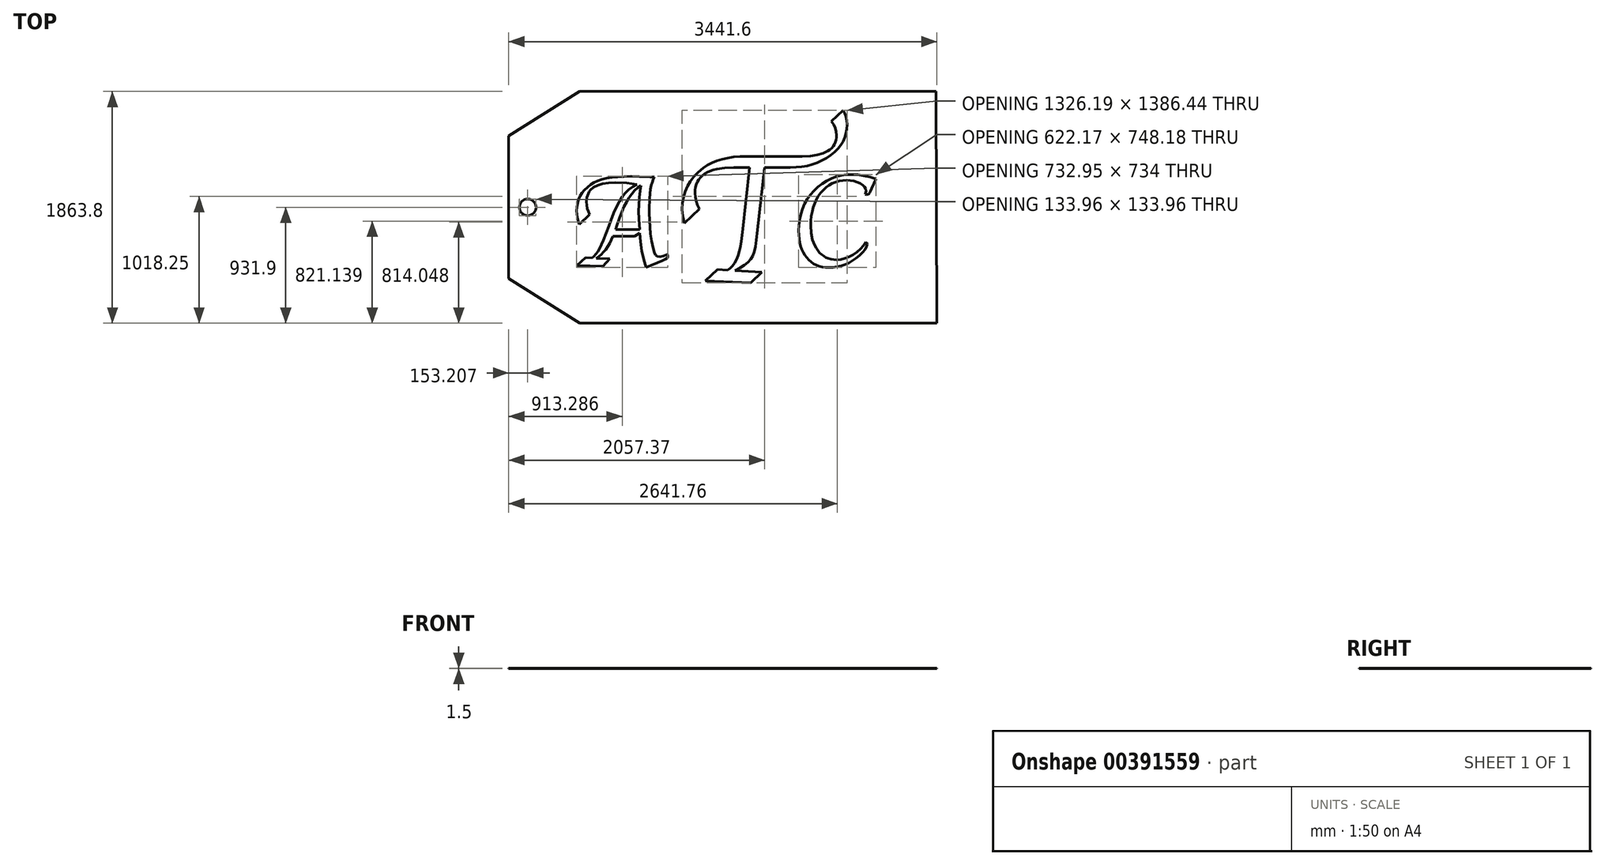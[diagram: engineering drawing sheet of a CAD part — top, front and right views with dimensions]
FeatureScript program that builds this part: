
annotation { "Feature Type Name" : "Feature", "Feature Type Description" : "" }
export const myFeature = defineFeature(function(context is Context, id is Id, definition is map)
    precondition{}
    {
        {
            var Q0;
            Q0=qCreatedBy(makeId("Top.planeOp"),FACE);
            var sketch = newSketch(context, id + "F0", { "sketchPlane" : qUnion([Q0])});
            skLineSegment(sketch, "E0", {"start": v(-1148.46, 931.9) * mm, "end": v(-1720.8, 573.48) * mm});
            skLineSegment(sketch, "E1", {"start": v(-1720.8, 573.48) * mm, "end": v(-1720.8, -573.48) * mm});
            skLineSegment(sketch, "E2", {"start": v(-1720.8, -573.48) * mm, "end": v(-1148.46, -931.9) * mm});
            skLineSegment(sketch, "E3", {"start": v(-1148.46, -931.9) * mm, "end": v(1720.8, -931.9) * mm});
            skLineSegment(sketch, "E4", {"start": v(1720.8, -931.9) * mm, "end": v(1714.81, 931.9) * mm});
            skLineSegment(sketch, "E5", {"start": v(1714.81, 931.9) * mm, "end": v(-1148.46, 931.9) * mm});
            skLineSegment(sketch, "E6", {"start": v(966.93, 779.57) * mm, "end": v(981.25, 755.67) * mm});
            skLineSegment(sketch, "E7", {"start": v(981.25, 755.67) * mm, "end": v(991.48, 728.62) * mm});
            skLineSegment(sketch, "E8", {"start": v(991.48, 728.62) * mm, "end": v(997.62, 698.4) * mm});
            skLineSegment(sketch, "E9", {"start": v(997.62, 698.4) * mm, "end": v(999.66, 665.03) * mm});
            skLineSegment(sketch, "E10", {"start": v(999.66, 665.03) * mm, "end": v(997.6, 629.13) * mm});
            skLineSegment(sketch, "E11", {"start": v(997.6, 629.13) * mm, "end": v(991.39, 594.7) * mm});
            skLineSegment(sketch, "E12", {"start": v(991.39, 594.7) * mm, "end": v(981.04, 561.72) * mm});
            skLineSegment(sketch, "E13", {"start": v(981.04, 561.72) * mm, "end": v(966.56, 530.2) * mm});
            skLineSegment(sketch, "E14", {"start": v(966.56, 530.2) * mm, "end": v(947.94, 500.17) * mm});
            skLineSegment(sketch, "E15", {"start": v(947.94, 500.17) * mm, "end": v(925.18, 471.59) * mm});
            skLineSegment(sketch, "E16", {"start": v(925.18, 471.59) * mm, "end": v(898.29, 444.47) * mm});
            skLineSegment(sketch, "E17", {"start": v(898.29, 444.47) * mm, "end": v(867.26, 418.82) * mm});
            skLineSegment(sketch, "E18", {"start": v(867.26, 418.82) * mm, "end": v(833.37, 395.64) * mm});
            skLineSegment(sketch, "E19", {"start": v(833.37, 395.64) * mm, "end": v(797.53, 375.54) * mm});
            skLineSegment(sketch, "E20", {"start": v(797.53, 375.54) * mm, "end": v(759.73, 358.54) * mm});
            skLineSegment(sketch, "E21", {"start": v(759.73, 358.54) * mm, "end": v(719.99, 344.63) * mm});
            skLineSegment(sketch, "E22", {"start": v(719.99, 344.63) * mm, "end": v(678.3, 333.81) * mm});
            skLineSegment(sketch, "E23", {"start": v(678.3, 333.81) * mm, "end": v(634.64, 326.09) * mm});
            skLineSegment(sketch, "E24", {"start": v(634.64, 326.09) * mm, "end": v(589.04, 321.45) * mm});
            skLineSegment(sketch, "E25", {"start": v(589.04, 321.45) * mm, "end": v(541.48, 319.9) * mm});
            skLineSegment(sketch, "E26", {"start": v(541.48, 319.9) * mm, "end": v(334.7, 319.9) * mm});
            skLineSegment(sketch, "E27", {"start": v(334.7, 319.9) * mm, "end": v(278.93, -182.9) * mm});
            skLineSegment(sketch, "E28", {"start": v(278.93, -182.9) * mm, "end": v(270, -265.47) * mm});
            skLineSegment(sketch, "E29", {"start": v(270, -265.47) * mm, "end": v(262.37, -314.6) * mm});
            skLineSegment(sketch, "E30", {"start": v(262.37, -314.6) * mm, "end": v(252.14, -356.4) * mm});
            skLineSegment(sketch, "E31", {"start": v(252.14, -356.4) * mm, "end": v(239.3, -390.84) * mm});
            skLineSegment(sketch, "E32", {"start": v(239.3, -390.84) * mm, "end": v(223.87, -417.94) * mm});
            skLineSegment(sketch, "E33", {"start": v(223.87, -417.94) * mm, "end": v(203.65, -441.23) * mm});
            skLineSegment(sketch, "E34", {"start": v(203.65, -441.23) * mm, "end": v(175.72, -464.25) * mm});
            skLineSegment(sketch, "E35", {"start": v(175.72, -464.25) * mm, "end": v(140.06, -486.98) * mm});
            skLineSegment(sketch, "E36", {"start": v(140.06, -486.98) * mm, "end": v(96.7, -509.44) * mm});
            skLineSegment(sketch, "E37", {"start": v(96.7, -509.44) * mm, "end": v(313.13, -520.6) * mm});
            skLineSegment(sketch, "E38", {"start": v(313.13, -520.6) * mm, "end": v(223.87, -606.87) * mm});
            skLineSegment(sketch, "E39", {"start": v(223.87, -606.87) * mm, "end": v(-139.1, -590.5) * mm});
            skLineSegment(sketch, "E40", {"start": v(-139.1, -590.5) * mm, "end": v(-43.15, -498.28) * mm});
            skLineSegment(sketch, "E41", {"start": v(-43.15, -498.28) * mm, "end": v(37.93, -507.2) * mm});
            skLineSegment(sketch, "E42", {"start": v(37.93, -507.2) * mm, "end": v(59.36, -491) * mm});
            skLineSegment(sketch, "E43", {"start": v(59.36, -491) * mm, "end": v(78.65, -471.08) * mm});
            skLineSegment(sketch, "E44", {"start": v(78.65, -471.08) * mm, "end": v(95.8, -447.4) * mm});
            skLineSegment(sketch, "E45", {"start": v(95.8, -447.4) * mm, "end": v(110.82, -419.99) * mm});
            skLineSegment(sketch, "E46", {"start": v(110.82, -419.99) * mm, "end": v(123.7, -388.83) * mm});
            skLineSegment(sketch, "E47", {"start": v(123.7, -388.83) * mm, "end": v(134.44, -353.93) * mm});
            skLineSegment(sketch, "E48", {"start": v(134.44, -353.93) * mm, "end": v(143.04, -315.29) * mm});
            skLineSegment(sketch, "E49", {"start": v(143.04, -315.29) * mm, "end": v(149.5, -272.9) * mm});
            skLineSegment(sketch, "E50", {"start": v(149.5, -272.9) * mm, "end": v(156.94, -200.76) * mm});
            skLineSegment(sketch, "E51", {"start": v(156.94, -200.76) * mm, "end": v(214.96, 319.9) * mm});
            skLineSegment(sketch, "E52", {"start": v(214.96, 319.9) * mm, "end": v(88.51, 319.9) * mm});
            skLineSegment(sketch, "E53", {"start": v(88.51, 319.9) * mm, "end": v(15.47, 316.69) * mm});
            skLineSegment(sketch, "E54", {"start": v(15.47, 316.69) * mm, "end": v(-47.84, 307.03) * mm});
            skLineSegment(sketch, "E55", {"start": v(-47.84, 307.03) * mm, "end": v(-75.84, 299.78) * mm});
            skLineSegment(sketch, "E56", {"start": v(-75.84, 299.78) * mm, "end": v(-101.4, 290.93) * mm});
            skLineSegment(sketch, "E57", {"start": v(-101.4, 290.93) * mm, "end": v(-124.53, 280.47) * mm});
            skLineSegment(sketch, "E58", {"start": v(-124.53, 280.47) * mm, "end": v(-145.23, 268.4) * mm});
            skLineSegment(sketch, "E59", {"start": v(-145.23, 268.4) * mm, "end": v(-163.5, 254.71) * mm});
            skLineSegment(sketch, "E60", {"start": v(-163.5, 254.71) * mm, "end": v(-179.32, 239.42) * mm});
            skLineSegment(sketch, "E61", {"start": v(-179.32, 239.42) * mm, "end": v(-192.7, 222.52) * mm});
            skLineSegment(sketch, "E62", {"start": v(-192.7, 222.52) * mm, "end": v(-203.67, 204) * mm});
            skLineSegment(sketch, "E63", {"start": v(-203.67, 204) * mm, "end": v(-212.19, 183.89) * mm});
            skLineSegment(sketch, "E64", {"start": v(-212.19, 183.89) * mm, "end": v(-218.28, 162.16) * mm});
            skLineSegment(sketch, "E65", {"start": v(-218.28, 162.16) * mm, "end": v(-221.93, 138.82) * mm});
            skLineSegment(sketch, "E66", {"start": v(-221.93, 138.82) * mm, "end": v(-223.15, 113.87) * mm});
            skLineSegment(sketch, "E67", {"start": v(-223.15, 113.87) * mm, "end": v(-220.96, 82.5) * mm});
            skLineSegment(sketch, "E68", {"start": v(-220.96, 82.5) * mm, "end": v(-214.4, 50.83) * mm});
            skLineSegment(sketch, "E69", {"start": v(-214.4, 50.83) * mm, "end": v(-203.48, 18.9) * mm});
            skLineSegment(sketch, "E70", {"start": v(-203.48, 18.9) * mm, "end": v(-188.19, -13.31) * mm});
            skLineSegment(sketch, "E71", {"start": v(-188.19, -13.31) * mm, "end": v(-309.42, -129.35) * mm});
            skLineSegment(sketch, "E72", {"start": v(-309.42, -129.35) * mm, "end": v(-322.25, -71.9) * mm});
            skLineSegment(sketch, "E73", {"start": v(-322.25, -71.9) * mm, "end": v(-326.53, -15.55) * mm});
            skLineSegment(sketch, "E74", {"start": v(-326.53, -15.55) * mm, "end": v(-323.87, 34.36) * mm});
            skLineSegment(sketch, "E75", {"start": v(-323.87, 34.36) * mm, "end": v(-315.88, 81.84) * mm});
            skLineSegment(sketch, "E76", {"start": v(-315.88, 81.84) * mm, "end": v(-302.58, 126.87) * mm});
            skLineSegment(sketch, "E77", {"start": v(-302.58, 126.87) * mm, "end": v(-283.95, 169.47) * mm});
            skLineSegment(sketch, "E78", {"start": v(-283.95, 169.47) * mm, "end": v(-260, 209.62) * mm});
            skLineSegment(sketch, "E79", {"start": v(-260, 209.62) * mm, "end": v(-230.73, 247.33) * mm});
            skLineSegment(sketch, "E80", {"start": v(-230.73, 247.33) * mm, "end": v(-196.13, 282.6) * mm});
            skLineSegment(sketch, "E81", {"start": v(-196.13, 282.6) * mm, "end": v(-156.2, 315.44) * mm});
            skLineSegment(sketch, "E82", {"start": v(-156.2, 315.44) * mm, "end": v(-122.91, 337.58) * mm});
            skLineSegment(sketch, "E83", {"start": v(-122.91, 337.58) * mm, "end": v(-86.62, 356.77) * mm});
            skLineSegment(sketch, "E84", {"start": v(-86.62, 356.77) * mm, "end": v(-47.32, 373) * mm});
            skLineSegment(sketch, "E85", {"start": v(-47.32, 373) * mm, "end": v(-5.03, 386.29) * mm});
            skLineSegment(sketch, "E86", {"start": v(-5.03, 386.29) * mm, "end": v(40.26, 396.62) * mm});
            skLineSegment(sketch, "E87", {"start": v(40.26, 396.62) * mm, "end": v(88.55, 404) * mm});
            skLineSegment(sketch, "E88", {"start": v(88.55, 404) * mm, "end": v(139.84, 408.43) * mm});
            skLineSegment(sketch, "E89", {"start": v(139.84, 408.43) * mm, "end": v(194.12, 409.9) * mm});
            skLineSegment(sketch, "E90", {"start": v(194.12, 409.9) * mm, "end": v(638.17, 409.9) * mm});
            skLineSegment(sketch, "E91", {"start": v(638.17, 409.9) * mm, "end": v(702.85, 412.56) * mm});
            skLineSegment(sketch, "E92", {"start": v(702.85, 412.56) * mm, "end": v(758.9, 420.55) * mm});
            skLineSegment(sketch, "E93", {"start": v(758.9, 420.55) * mm, "end": v(806.33, 433.85) * mm});
            skLineSegment(sketch, "E94", {"start": v(806.33, 433.85) * mm, "end": v(845.13, 452.48) * mm});
            skLineSegment(sketch, "E95", {"start": v(845.13, 452.48) * mm, "end": v(861.3, 463.8) * mm});
            skLineSegment(sketch, "E96", {"start": v(861.3, 463.8) * mm, "end": v(875.31, 476.43) * mm});
            skLineSegment(sketch, "E97", {"start": v(875.31, 476.43) * mm, "end": v(887.17, 490.4) * mm});
            skLineSegment(sketch, "E98", {"start": v(887.17, 490.4) * mm, "end": v(896.87, 505.7) * mm});
            skLineSegment(sketch, "E99", {"start": v(896.87, 505.7) * mm, "end": v(904.42, 522.34) * mm});
            skLineSegment(sketch, "E100", {"start": v(904.42, 522.34) * mm, "end": v(909.8, 540.3) * mm});
            skLineSegment(sketch, "E101", {"start": v(909.8, 540.3) * mm, "end": v(913.04, 559.6) * mm});
            skLineSegment(sketch, "E102", {"start": v(913.04, 559.6) * mm, "end": v(914.12, 580.22) * mm});
            skLineSegment(sketch, "E103", {"start": v(914.12, 580.22) * mm, "end": v(911.56, 609.42) * mm});
            skLineSegment(sketch, "E104", {"start": v(911.56, 609.42) * mm, "end": v(903.89, 637.5) * mm});
            skLineSegment(sketch, "E105", {"start": v(903.89, 637.5) * mm, "end": v(891.1, 664.46) * mm});
            skLineSegment(sketch, "E106", {"start": v(891.1, 664.46) * mm, "end": v(873.2, 690.31) * mm});
            skLineSegment(sketch, "E107", {"start": v(873.2, 690.31) * mm, "end": v(966.93, 779.57) * mm});
            skLineSegment(sketch, "E108", {"start": v(1039.35, 263.33) * mm, "end": v(1086.25, 261.13) * mm});
            skLineSegment(sketch, "E109", {"start": v(1086.25, 261.13) * mm, "end": v(1134, 254.53) * mm});
            skLineSegment(sketch, "E110", {"start": v(1134, 254.53) * mm, "end": v(1182.6, 243.54) * mm});
            skLineSegment(sketch, "E111", {"start": v(1182.6, 243.54) * mm, "end": v(1232.05, 228.14) * mm});
            skLineSegment(sketch, "E112", {"start": v(1232.05, 228.14) * mm, "end": v(1196.86, 150.97) * mm});
            skLineSegment(sketch, "E113", {"start": v(1196.86, 150.97) * mm, "end": v(1186.9, 128.39) * mm});
            skLineSegment(sketch, "E114", {"start": v(1186.9, 128.39) * mm, "end": v(1180.23, 116.67) * mm});
            skLineSegment(sketch, "E115", {"start": v(1180.23, 116.67) * mm, "end": v(1172.85, 108.3) * mm});
            skLineSegment(sketch, "E116", {"start": v(1172.85, 108.3) * mm, "end": v(1164.74, 103.3) * mm});
            skLineSegment(sketch, "E117", {"start": v(1164.74, 103.3) * mm, "end": v(1155.91, 101.62) * mm});
            skLineSegment(sketch, "E118", {"start": v(1155.91, 101.62) * mm, "end": v(1144.9, 103.19) * mm});
            skLineSegment(sketch, "E119", {"start": v(1144.9, 103.19) * mm, "end": v(1150.4, 118.02) * mm});
            skLineSegment(sketch, "E120", {"start": v(1150.4, 118.02) * mm, "end": v(1152.24, 129.97) * mm});
            skLineSegment(sketch, "E121", {"start": v(1152.24, 129.97) * mm, "end": v(1149.3, 147) * mm});
            skLineSegment(sketch, "E122", {"start": v(1149.3, 147) * mm, "end": v(1140.43, 162.91) * mm});
            skLineSegment(sketch, "E123", {"start": v(1140.43, 162.91) * mm, "end": v(1125.66, 177.7) * mm});
            skLineSegment(sketch, "E124", {"start": v(1125.66, 177.7) * mm, "end": v(1105, 191.4) * mm});
            skLineSegment(sketch, "E125", {"start": v(1105, 191.4) * mm, "end": v(1080.64, 202.88) * mm});
            skLineSegment(sketch, "E126", {"start": v(1080.64, 202.88) * mm, "end": v(1054.32, 211.08) * mm});
            skLineSegment(sketch, "E127", {"start": v(1054.32, 211.08) * mm, "end": v(1026.04, 216) * mm});
            skLineSegment(sketch, "E128", {"start": v(1026.04, 216) * mm, "end": v(995.78, 217.64) * mm});
            skLineSegment(sketch, "E129", {"start": v(995.78, 217.64) * mm, "end": v(964.5, 216.06) * mm});
            skLineSegment(sketch, "E130", {"start": v(964.5, 216.06) * mm, "end": v(934.71, 211.31) * mm});
            skLineSegment(sketch, "E131", {"start": v(934.71, 211.31) * mm, "end": v(906.42, 203.4) * mm});
            skLineSegment(sketch, "E132", {"start": v(906.42, 203.4) * mm, "end": v(879.62, 192.31) * mm});
            skLineSegment(sketch, "E133", {"start": v(879.62, 192.31) * mm, "end": v(854.3, 178.07) * mm});
            skLineSegment(sketch, "E134", {"start": v(854.3, 178.07) * mm, "end": v(830.5, 160.65) * mm});
            skLineSegment(sketch, "E135", {"start": v(830.5, 160.65) * mm, "end": v(808.17, 140.07) * mm});
            skLineSegment(sketch, "E136", {"start": v(808.17, 140.07) * mm, "end": v(787.34, 116.32) * mm});
            skLineSegment(sketch, "E137", {"start": v(787.34, 116.32) * mm, "end": v(768.63, 90.03) * mm});
            skLineSegment(sketch, "E138", {"start": v(768.63, 90.03) * mm, "end": v(752.42, 61.85) * mm});
            skLineSegment(sketch, "E139", {"start": v(752.42, 61.85) * mm, "end": v(738.7, 31.76) * mm});
            skLineSegment(sketch, "E140", {"start": v(738.7, 31.76) * mm, "end": v(727.49, -0.24) * mm});
            skLineSegment(sketch, "E141", {"start": v(727.49, -0.24) * mm, "end": v(718.76, -34.14) * mm});
            skLineSegment(sketch, "E142", {"start": v(718.76, -34.14) * mm, "end": v(712.52, -69.94) * mm});
            skLineSegment(sketch, "E143", {"start": v(712.52, -69.94) * mm, "end": v(708.78, -107.64) * mm});
            skLineSegment(sketch, "E144", {"start": v(708.78, -107.64) * mm, "end": v(707.53, -147.25) * mm});
            skLineSegment(sketch, "E145", {"start": v(707.53, -147.25) * mm, "end": v(711.05, -206.8) * mm});
            skLineSegment(sketch, "E146", {"start": v(711.05, -206.8) * mm, "end": v(721.58, -260) * mm});
            skLineSegment(sketch, "E147", {"start": v(721.58, -260) * mm, "end": v(729.48, -284.21) * mm});
            skLineSegment(sketch, "E148", {"start": v(729.48, -284.21) * mm, "end": v(739.14, -306.83) * mm});
            skLineSegment(sketch, "E149", {"start": v(739.14, -306.83) * mm, "end": v(750.55, -327.86) * mm});
            skLineSegment(sketch, "E150", {"start": v(750.55, -327.86) * mm, "end": v(763.72, -347.3) * mm});
            skLineSegment(sketch, "E151", {"start": v(763.72, -347.3) * mm, "end": v(778.35, -364.77) * mm});
            skLineSegment(sketch, "E152", {"start": v(778.35, -364.77) * mm, "end": v(794.17, -379.9) * mm});
            skLineSegment(sketch, "E153", {"start": v(794.17, -379.9) * mm, "end": v(811.17, -392.72) * mm});
            skLineSegment(sketch, "E154", {"start": v(811.17, -392.72) * mm, "end": v(829.35, -403.2) * mm});
            skLineSegment(sketch, "E155", {"start": v(829.35, -403.2) * mm, "end": v(848.7, -411.36) * mm});
            skLineSegment(sketch, "E156", {"start": v(848.7, -411.36) * mm, "end": v(869.25, -417.19) * mm});
            skLineSegment(sketch, "E157", {"start": v(869.25, -417.19) * mm, "end": v(890.97, -420.68) * mm});
            skLineSegment(sketch, "E158", {"start": v(890.97, -420.68) * mm, "end": v(913.88, -421.85) * mm});
            skLineSegment(sketch, "E159", {"start": v(913.88, -421.85) * mm, "end": v(947.7, -419.32) * mm});
            skLineSegment(sketch, "E160", {"start": v(947.7, -419.32) * mm, "end": v(981.47, -411.74) * mm});
            skLineSegment(sketch, "E161", {"start": v(981.47, -411.74) * mm, "end": v(1015.17, -399.1) * mm});
            skLineSegment(sketch, "E162", {"start": v(1015.17, -399.1) * mm, "end": v(1048.8, -381.41) * mm});
            skLineSegment(sketch, "E163", {"start": v(1048.8, -381.41) * mm, "end": v(1080.44, -359.75) * mm});
            skLineSegment(sketch, "E164", {"start": v(1080.44, -359.75) * mm, "end": v(1107.6, -335.73) * mm});
            skLineSegment(sketch, "E165", {"start": v(1107.6, -335.73) * mm, "end": v(1130.32, -309.35) * mm});
            skLineSegment(sketch, "E166", {"start": v(1130.32, -309.35) * mm, "end": v(1148.56, -280.6) * mm});
            skLineSegment(sketch, "E167", {"start": v(1148.56, -280.6) * mm, "end": v(1157.62, -287.7) * mm});
            skLineSegment(sketch, "E168", {"start": v(1157.62, -287.7) * mm, "end": v(1160.64, -297.4) * mm});
            skLineSegment(sketch, "E169", {"start": v(1160.64, -297.4) * mm, "end": v(1156.67, -316.11) * mm});
            skLineSegment(sketch, "E170", {"start": v(1156.67, -316.11) * mm, "end": v(1144.76, -337.57) * mm});
            skLineSegment(sketch, "E171", {"start": v(1144.76, -337.57) * mm, "end": v(1124.9, -361.79) * mm});
            skLineSegment(sketch, "E172", {"start": v(1124.9, -361.79) * mm, "end": v(1097.1, -388.76) * mm});
            skLineSegment(sketch, "E173", {"start": v(1097.1, -388.76) * mm, "end": v(1069.74, -411.28) * mm});
            skLineSegment(sketch, "E174", {"start": v(1069.74, -411.28) * mm, "end": v(1041.45, -430.8) * mm});
            skLineSegment(sketch, "E175", {"start": v(1041.45, -430.8) * mm, "end": v(1012.25, -447.31) * mm});
            skLineSegment(sketch, "E176", {"start": v(1012.25, -447.31) * mm, "end": v(982.13, -460.83) * mm});
            skLineSegment(sketch, "E177", {"start": v(982.13, -460.83) * mm, "end": v(951.08, -471.34) * mm});
            skLineSegment(sketch, "E178", {"start": v(951.08, -471.34) * mm, "end": v(919.12, -478.84) * mm});
            skLineSegment(sketch, "E179", {"start": v(919.12, -478.84) * mm, "end": v(886.24, -483.35) * mm});
            skLineSegment(sketch, "E180", {"start": v(886.24, -483.35) * mm, "end": v(852.44, -484.85) * mm});
            skLineSegment(sketch, "E181", {"start": v(852.44, -484.85) * mm, "end": v(825.44, -483.6) * mm});
            skLineSegment(sketch, "E182", {"start": v(825.44, -483.6) * mm, "end": v(799.84, -479.86) * mm});
            skLineSegment(sketch, "E183", {"start": v(799.84, -479.86) * mm, "end": v(775.63, -473.63) * mm});
            skLineSegment(sketch, "E184", {"start": v(775.63, -473.63) * mm, "end": v(752.82, -464.9) * mm});
            skLineSegment(sketch, "E185", {"start": v(752.82, -464.9) * mm, "end": v(731.4, -453.68) * mm});
            skLineSegment(sketch, "E186", {"start": v(731.4, -453.68) * mm, "end": v(711.38, -439.96) * mm});
            skLineSegment(sketch, "E187", {"start": v(711.38, -439.96) * mm, "end": v(692.75, -423.75) * mm});
            skLineSegment(sketch, "E188", {"start": v(692.75, -423.75) * mm, "end": v(675.51, -405.05) * mm});
            skLineSegment(sketch, "E189", {"start": v(675.51, -405.05) * mm, "end": v(660.13, -384.1) * mm});
            skLineSegment(sketch, "E190", {"start": v(660.13, -384.1) * mm, "end": v(646.8, -361.47) * mm});
            skLineSegment(sketch, "E191", {"start": v(646.8, -361.47) * mm, "end": v(635.52, -337.12) * mm});
            skLineSegment(sketch, "E192", {"start": v(635.52, -337.12) * mm, "end": v(626.29, -311.06) * mm});
            skLineSegment(sketch, "E193", {"start": v(626.29, -311.06) * mm, "end": v(619.1, -283.3) * mm});
            skLineSegment(sketch, "E194", {"start": v(619.1, -283.3) * mm, "end": v(613.98, -253.84) * mm});
            skLineSegment(sketch, "E195", {"start": v(613.98, -253.84) * mm, "end": v(610.9, -222.66) * mm});
            skLineSegment(sketch, "E196", {"start": v(610.9, -222.66) * mm, "end": v(609.88, -189.78) * mm});
            skLineSegment(sketch, "E197", {"start": v(609.88, -189.78) * mm, "end": v(611.8, -142.59) * mm});
            skLineSegment(sketch, "E198", {"start": v(611.8, -142.59) * mm, "end": v(617.6, -97.34) * mm});
            skLineSegment(sketch, "E199", {"start": v(617.6, -97.34) * mm, "end": v(627.23, -54.05) * mm});
            skLineSegment(sketch, "E200", {"start": v(627.23, -54.05) * mm, "end": v(640.73, -12.71) * mm});
            skLineSegment(sketch, "E201", {"start": v(640.73, -12.71) * mm, "end": v(658.08, 26.68) * mm});
            skLineSegment(sketch, "E202", {"start": v(658.08, 26.68) * mm, "end": v(679.29, 64.11) * mm});
            skLineSegment(sketch, "E203", {"start": v(679.29, 64.11) * mm, "end": v(704.35, 99.6) * mm});
            skLineSegment(sketch, "E204", {"start": v(704.35, 99.6) * mm, "end": v(733.27, 133.12) * mm});
            skLineSegment(sketch, "E205", {"start": v(733.27, 133.12) * mm, "end": v(765.04, 163.64) * mm});
            skLineSegment(sketch, "E206", {"start": v(765.04, 163.64) * mm, "end": v(798.67, 190.09) * mm});
            skLineSegment(sketch, "E207", {"start": v(798.67, 190.09) * mm, "end": v(834.15, 212.47) * mm});
            skLineSegment(sketch, "E208", {"start": v(834.15, 212.47) * mm, "end": v(871.48, 230.78) * mm});
            skLineSegment(sketch, "E209", {"start": v(871.48, 230.78) * mm, "end": v(910.67, 245.02) * mm});
            skLineSegment(sketch, "E210", {"start": v(910.67, 245.02) * mm, "end": v(951.7, 255.2) * mm});
            skLineSegment(sketch, "E211", {"start": v(951.7, 255.2) * mm, "end": v(994.6, 261.3) * mm});
            skLineSegment(sketch, "E212", {"start": v(994.6, 261.3) * mm, "end": v(1039.35, 263.33) * mm});
            skLineSegment(sketch, "E213", {"start": v(-737.68, 249.15) * mm, "end": v(-669.42, 247.58) * mm});
            skLineSegment(sketch, "E214", {"start": v(-669.42, 247.58) * mm, "end": v(-585.95, 242.33) * mm});
            skLineSegment(sketch, "E215", {"start": v(-585.95, 242.33) * mm, "end": v(-549.2, 242.33) * mm});
            skLineSegment(sketch, "E216", {"start": v(-549.2, 242.33) * mm, "end": v(-558.8, 224.26) * mm});
            skLineSegment(sketch, "E217", {"start": v(-558.8, 224.26) * mm, "end": v(-567.11, 202.1) * mm});
            skLineSegment(sketch, "E218", {"start": v(-567.11, 202.1) * mm, "end": v(-574.15, 175.83) * mm});
            skLineSegment(sketch, "E219", {"start": v(-574.15, 175.83) * mm, "end": v(-579.91, 145.46) * mm});
            skLineSegment(sketch, "E220", {"start": v(-579.91, 145.46) * mm, "end": v(-587.6, 72.41) * mm});
            skLineSegment(sketch, "E221", {"start": v(-587.6, 72.41) * mm, "end": v(-590.15, -17.04) * mm});
            skLineSegment(sketch, "E222", {"start": v(-590.15, -17.04) * mm, "end": v(-589.62, -44.34) * mm});
            skLineSegment(sketch, "E223", {"start": v(-589.62, -44.34) * mm, "end": v(-587.52, -104.73) * mm});
            skLineSegment(sketch, "E224", {"start": v(-587.52, -104.73) * mm, "end": v(-585.85, -159.4) * mm});
            skLineSegment(sketch, "E225", {"start": v(-585.85, -159.4) * mm, "end": v(-580.83, -214.72) * mm});
            skLineSegment(sketch, "E226", {"start": v(-580.83, -214.72) * mm, "end": v(-572.46, -270.7) * mm});
            skLineSegment(sketch, "E227", {"start": v(-572.46, -270.7) * mm, "end": v(-560.75, -327.34) * mm});
            skLineSegment(sketch, "E228", {"start": v(-560.75, -327.34) * mm, "end": v(-550.38, -363.57) * mm});
            skLineSegment(sketch, "E229", {"start": v(-550.38, -363.57) * mm, "end": v(-540.27, -384.04) * mm});
            skLineSegment(sketch, "E230", {"start": v(-540.27, -384.04) * mm, "end": v(-534.36, -389.56) * mm});
            skLineSegment(sketch, "E231", {"start": v(-534.36, -389.56) * mm, "end": v(-526.61, -393.5) * mm});
            skLineSegment(sketch, "E232", {"start": v(-526.61, -393.5) * mm, "end": v(-505.61, -396.64) * mm});
            skLineSegment(sketch, "E233", {"start": v(-505.61, -396.64) * mm, "end": v(-477, -392.3) * mm});
            skLineSegment(sketch, "E234", {"start": v(-477, -392.3) * mm, "end": v(-444.7, -379.31) * mm});
            skLineSegment(sketch, "E235", {"start": v(-444.7, -379.31) * mm, "end": v(-441.04, -394.01) * mm});
            skLineSegment(sketch, "E236", {"start": v(-441.04, -394.01) * mm, "end": v(-442.32, -400.35) * mm});
            skLineSegment(sketch, "E237", {"start": v(-442.32, -400.35) * mm, "end": v(-446.16, -406.22) * mm});
            skLineSegment(sketch, "E238", {"start": v(-446.16, -406.22) * mm, "end": v(-461.51, -416.6) * mm});
            skLineSegment(sketch, "E239", {"start": v(-461.51, -416.6) * mm, "end": v(-486.2, -428.66) * mm});
            skLineSegment(sketch, "E240", {"start": v(-486.2, -428.66) * mm, "end": v(-615.35, -484.85) * mm});
            skLineSegment(sketch, "E241", {"start": v(-615.35, -484.85) * mm, "end": v(-634.74, -417.65) * mm});
            skLineSegment(sketch, "E242", {"start": v(-634.74, -417.65) * mm, "end": v(-649.87, -348.87) * mm});
            skLineSegment(sketch, "E243", {"start": v(-649.87, -348.87) * mm, "end": v(-660.73, -278.51) * mm});
            skLineSegment(sketch, "E244", {"start": v(-660.73, -278.51) * mm, "end": v(-667.32, -206.58) * mm});
            skLineSegment(sketch, "E245", {"start": v(-667.32, -206.58) * mm, "end": v(-707.23, -234.4) * mm});
            skLineSegment(sketch, "E246", {"start": v(-707.23, -234.4) * mm, "end": v(-883.64, -234.4) * mm});
            skLineSegment(sketch, "E247", {"start": v(-883.64, -234.4) * mm, "end": v(-910.02, -291.43) * mm});
            skLineSegment(sketch, "E248", {"start": v(-910.02, -291.43) * mm, "end": v(-940.87, -339.67) * mm});
            skLineSegment(sketch, "E249", {"start": v(-940.87, -339.67) * mm, "end": v(-957.96, -360.5) * mm});
            skLineSegment(sketch, "E250", {"start": v(-957.96, -360.5) * mm, "end": v(-976.17, -379.11) * mm});
            skLineSegment(sketch, "E251", {"start": v(-976.17, -379.11) * mm, "end": v(-995.5, -395.54) * mm});
            skLineSegment(sketch, "E252", {"start": v(-995.5, -395.54) * mm, "end": v(-1015.95, -409.76) * mm});
            skLineSegment(sketch, "E253", {"start": v(-1015.95, -409.76) * mm, "end": v(-907.27, -415.01) * mm});
            skLineSegment(sketch, "E254", {"start": v(-907.27, -415.01) * mm, "end": v(-963.97, -474.87) * mm});
            skLineSegment(sketch, "E255", {"start": v(-963.97, -474.87) * mm, "end": v(-1173.45, -467.52) * mm});
            skLineSegment(sketch, "E256", {"start": v(-1173.45, -467.52) * mm, "end": v(-1103.63, -404.51) * mm});
            skLineSegment(sketch, "E257", {"start": v(-1103.63, -404.51) * mm, "end": v(-1051.13, -407.66) * mm});
            skLineSegment(sketch, "E258", {"start": v(-1051.13, -407.66) * mm, "end": v(-1033.93, -393.22) * mm});
            skLineSegment(sketch, "E259", {"start": v(-1033.93, -393.22) * mm, "end": v(-1018.05, -376.16) * mm});
            skLineSegment(sketch, "E260", {"start": v(-1018.05, -376.16) * mm, "end": v(-1003.48, -356.47) * mm});
            skLineSegment(sketch, "E261", {"start": v(-1003.48, -356.47) * mm, "end": v(-990.23, -334.16) * mm});
            skLineSegment(sketch, "E262", {"start": v(-990.23, -334.16) * mm, "end": v(-958.85, -264.2) * mm});
            skLineSegment(sketch, "E263", {"start": v(-958.85, -264.2) * mm, "end": v(-915.14, -149.88) * mm});
            skLineSegment(sketch, "E264", {"start": v(-915.14, -149.88) * mm, "end": v(-899.39, -106.3) * mm});
            skLineSegment(sketch, "E265", {"start": v(-899.39, -106.3) * mm, "end": v(-875.53, -44.9) * mm});
            skLineSegment(sketch, "E266", {"start": v(-875.53, -44.9) * mm, "end": v(-852.27, 7.5) * mm});
            skLineSegment(sketch, "E267", {"start": v(-852.27, 7.5) * mm, "end": v(-829.6, 50.91) * mm});
            skLineSegment(sketch, "E268", {"start": v(-829.6, 50.91) * mm, "end": v(-807.51, 85.34) * mm});
            skLineSegment(sketch, "E269", {"start": v(-807.51, 85.34) * mm, "end": v(-783.76, 114.18) * mm});
            skLineSegment(sketch, "E270", {"start": v(-783.76, 114.18) * mm, "end": v(-756.06, 140.34) * mm});
            skLineSegment(sketch, "E271", {"start": v(-756.06, 140.34) * mm, "end": v(-724.43, 163.8) * mm});
            skLineSegment(sketch, "E272", {"start": v(-724.43, 163.8) * mm, "end": v(-688.86, 184.57) * mm});
            skLineSegment(sketch, "E273", {"start": v(-688.86, 184.57) * mm, "end": v(-773.51, 195.99) * mm});
            skLineSegment(sketch, "E274", {"start": v(-773.51, 195.99) * mm, "end": v(-862.64, 199.8) * mm});
            skLineSegment(sketch, "E275", {"start": v(-862.64, 199.8) * mm, "end": v(-917.15, 197.34) * mm});
            skLineSegment(sketch, "E276", {"start": v(-917.15, 197.34) * mm, "end": v(-964.4, 189.98) * mm});
            skLineSegment(sketch, "E277", {"start": v(-964.4, 189.98) * mm, "end": v(-1004.37, 177.72) * mm});
            skLineSegment(sketch, "E278", {"start": v(-1004.37, 177.72) * mm, "end": v(-1037.08, 160.55) * mm});
            skLineSegment(sketch, "E279", {"start": v(-1037.08, 160.55) * mm, "end": v(-1062.52, 138.48) * mm});
            skLineSegment(sketch, "E280", {"start": v(-1062.52, 138.48) * mm, "end": v(-1072.52, 125.6) * mm});
            skLineSegment(sketch, "E281", {"start": v(-1072.52, 125.6) * mm, "end": v(-1080.7, 111.5) * mm});
            skLineSegment(sketch, "E282", {"start": v(-1080.7, 111.5) * mm, "end": v(-1091.6, 79.6) * mm});
            skLineSegment(sketch, "E283", {"start": v(-1091.6, 79.6) * mm, "end": v(-1095.23, 42.81) * mm});
            skLineSegment(sketch, "E284", {"start": v(-1095.23, 42.81) * mm, "end": v(-1093.66, 16.46) * mm});
            skLineSegment(sketch, "E285", {"start": v(-1093.66, 16.46) * mm, "end": v(-1088.93, -9.04) * mm});
            skLineSegment(sketch, "E286", {"start": v(-1088.93, -9.04) * mm, "end": v(-1081.06, -33.68) * mm});
            skLineSegment(sketch, "E287", {"start": v(-1081.06, -33.68) * mm, "end": v(-1070.03, -57.47) * mm});
            skLineSegment(sketch, "E288", {"start": v(-1070.03, -57.47) * mm, "end": v(-1152.45, -136.75) * mm});
            skLineSegment(sketch, "E289", {"start": v(-1152.45, -136.75) * mm, "end": v(-1161.87, -108.89) * mm});
            skLineSegment(sketch, "E290", {"start": v(-1161.87, -108.89) * mm, "end": v(-1168.6, -81.5) * mm});
            skLineSegment(sketch, "E291", {"start": v(-1168.6, -81.5) * mm, "end": v(-1172.64, -54.55) * mm});
            skLineSegment(sketch, "E292", {"start": v(-1172.64, -54.55) * mm, "end": v(-1173.99, -28.07) * mm});
            skLineSegment(sketch, "E293", {"start": v(-1173.99, -28.07) * mm, "end": v(-1172.22, 3.7) * mm});
            skLineSegment(sketch, "E294", {"start": v(-1172.22, 3.7) * mm, "end": v(-1166.93, 33.88) * mm});
            skLineSegment(sketch, "E295", {"start": v(-1166.93, 33.88) * mm, "end": v(-1158.11, 62.5) * mm});
            skLineSegment(sketch, "E296", {"start": v(-1158.11, 62.5) * mm, "end": v(-1145.76, 89.54) * mm});
            skLineSegment(sketch, "E297", {"start": v(-1145.76, 89.54) * mm, "end": v(-1129.89, 115) * mm});
            skLineSegment(sketch, "E298", {"start": v(-1129.89, 115) * mm, "end": v(-1110.48, 138.89) * mm});
            skLineSegment(sketch, "E299", {"start": v(-1110.48, 138.89) * mm, "end": v(-1087.55, 161.2) * mm});
            skLineSegment(sketch, "E300", {"start": v(-1087.55, 161.2) * mm, "end": v(-1061.1, 181.94) * mm});
            skLineSegment(sketch, "E301", {"start": v(-1061.1, 181.94) * mm, "end": v(-1035.37, 197.7) * mm});
            skLineSegment(sketch, "E302", {"start": v(-1035.37, 197.7) * mm, "end": v(-1005.44, 211.34) * mm});
            skLineSegment(sketch, "E303", {"start": v(-1005.44, 211.34) * mm, "end": v(-971.32, 222.9) * mm});
            skLineSegment(sketch, "E304", {"start": v(-971.32, 222.9) * mm, "end": v(-932.99, 232.34) * mm});
            skLineSegment(sketch, "E305", {"start": v(-932.99, 232.34) * mm, "end": v(-890.46, 239.7) * mm});
            skLineSegment(sketch, "E306", {"start": v(-890.46, 239.7) * mm, "end": v(-843.73, 244.95) * mm});
            skLineSegment(sketch, "E307", {"start": v(-843.73, 244.95) * mm, "end": v(-792.8, 248.1) * mm});
            skLineSegment(sketch, "E308", {"start": v(-792.8, 248.1) * mm, "end": v(-737.68, 249.15) * mm});
            skLineSegment(sketch, "E309", {"start": v(-658.92, 174.07) * mm, "end": v(-684.08, 156.27) * mm});
            skLineSegment(sketch, "E310", {"start": v(-684.08, 156.27) * mm, "end": v(-708.08, 134.37) * mm});
            skLineSegment(sketch, "E311", {"start": v(-708.08, 134.37) * mm, "end": v(-730.93, 108.36) * mm});
            skLineSegment(sketch, "E312", {"start": v(-730.93, 108.36) * mm, "end": v(-752.64, 78.25) * mm});
            skLineSegment(sketch, "E313", {"start": v(-752.64, 78.25) * mm, "end": v(-773.2, 44.05) * mm});
            skLineSegment(sketch, "E314", {"start": v(-773.2, 44.05) * mm, "end": v(-792.6, 5.73) * mm});
            skLineSegment(sketch, "E315", {"start": v(-792.6, 5.73) * mm, "end": v(-810.87, -36.68) * mm});
            skLineSegment(sketch, "E316", {"start": v(-810.87, -36.68) * mm, "end": v(-827.98, -83.2) * mm});
            skLineSegment(sketch, "E317", {"start": v(-827.98, -83.2) * mm, "end": v(-850.03, -147.78) * mm});
            skLineSegment(sketch, "E318", {"start": v(-850.03, -147.78) * mm, "end": v(-862.12, -177.7) * mm});
            skLineSegment(sketch, "E319", {"start": v(-862.12, -177.7) * mm, "end": v(-668.37, -177.7) * mm});
            skLineSegment(sketch, "E320", {"start": v(-668.37, -177.7) * mm, "end": v(-673.89, -95) * mm});
            skLineSegment(sketch, "E321", {"start": v(-673.89, -95) * mm, "end": v(-675.72, -29.64) * mm});
            skLineSegment(sketch, "E322", {"start": v(-675.72, -29.64) * mm, "end": v(-674.67, 17.61) * mm});
            skLineSegment(sketch, "E323", {"start": v(-674.67, 17.61) * mm, "end": v(-670.47, 78.52) * mm});
            skLineSegment(sketch, "E324", {"start": v(-670.47, 78.52) * mm, "end": v(-665.49, 133.65) * mm});
            skLineSegment(sketch, "E325", {"start": v(-665.49, 133.65) * mm, "end": v(-658.92, 174.07) * mm});
            skLineSegment(sketch, "E326", {"start": v(-1567.6, 66.98) * mm, "end": v(-1554.46, 65.68) * mm});
            skLineSegment(sketch, "E327", {"start": v(-1554.46, 65.68) * mm, "end": v(-1541.96, 61.88) * mm});
            skLineSegment(sketch, "E328", {"start": v(-1541.96, 61.88) * mm, "end": v(-1530.43, 55.73) * mm});
            skLineSegment(sketch, "E329", {"start": v(-1530.43, 55.73) * mm, "end": v(-1520.23, 47.36) * mm});
            skLineSegment(sketch, "E330", {"start": v(-1520.23, 47.36) * mm, "end": v(-1511.87, 37.16) * mm});
            skLineSegment(sketch, "E331", {"start": v(-1511.87, 37.16) * mm, "end": v(-1505.71, 25.63) * mm});
            skLineSegment(sketch, "E332", {"start": v(-1505.71, 25.63) * mm, "end": v(-1501.91, 13.13) * mm});
            skLineSegment(sketch, "E333", {"start": v(-1501.91, 13.13) * mm, "end": v(-1500.61, 0) * mm});
            skLineSegment(sketch, "E334", {"start": v(-1500.61, 0) * mm, "end": v(-1501.91, -13.13) * mm});
            skLineSegment(sketch, "E335", {"start": v(-1501.91, -13.13) * mm, "end": v(-1505.71, -25.63) * mm});
            skLineSegment(sketch, "E336", {"start": v(-1505.71, -25.63) * mm, "end": v(-1511.87, -37.16) * mm});
            skLineSegment(sketch, "E337", {"start": v(-1511.87, -37.16) * mm, "end": v(-1520.23, -47.36) * mm});
            skLineSegment(sketch, "E338", {"start": v(-1520.23, -47.36) * mm, "end": v(-1530.43, -55.73) * mm});
            skLineSegment(sketch, "E339", {"start": v(-1530.43, -55.73) * mm, "end": v(-1541.96, -61.88) * mm});
            skLineSegment(sketch, "E340", {"start": v(-1541.96, -61.88) * mm, "end": v(-1554.46, -65.68) * mm});
            skLineSegment(sketch, "E341", {"start": v(-1554.46, -65.68) * mm, "end": v(-1567.6, -66.98) * mm});
            skLineSegment(sketch, "E342", {"start": v(-1567.6, -66.98) * mm, "end": v(-1580.72, -65.68) * mm});
            skLineSegment(sketch, "E343", {"start": v(-1580.72, -65.68) * mm, "end": v(-1593.23, -61.88) * mm});
            skLineSegment(sketch, "E344", {"start": v(-1593.23, -61.88) * mm, "end": v(-1604.75, -55.73) * mm});
            skLineSegment(sketch, "E345", {"start": v(-1604.75, -55.73) * mm, "end": v(-1614.96, -47.36) * mm});
            skLineSegment(sketch, "E346", {"start": v(-1614.96, -47.36) * mm, "end": v(-1623.32, -37.16) * mm});
            skLineSegment(sketch, "E347", {"start": v(-1623.32, -37.16) * mm, "end": v(-1629.48, -25.63) * mm});
            skLineSegment(sketch, "E348", {"start": v(-1629.48, -25.63) * mm, "end": v(-1633.28, -13.13) * mm});
            skLineSegment(sketch, "E349", {"start": v(-1633.28, -13.13) * mm, "end": v(-1634.57, 0) * mm});
            skLineSegment(sketch, "E350", {"start": v(-1634.57, 0) * mm, "end": v(-1633.28, 13.13) * mm});
            skLineSegment(sketch, "E351", {"start": v(-1633.28, 13.13) * mm, "end": v(-1629.48, 25.63) * mm});
            skLineSegment(sketch, "E352", {"start": v(-1629.48, 25.63) * mm, "end": v(-1623.32, 37.16) * mm});
            skLineSegment(sketch, "E353", {"start": v(-1623.32, 37.16) * mm, "end": v(-1614.96, 47.36) * mm});
            skLineSegment(sketch, "E354", {"start": v(-1614.96, 47.36) * mm, "end": v(-1604.75, 55.73) * mm});
            skLineSegment(sketch, "E355", {"start": v(-1604.75, 55.73) * mm, "end": v(-1593.23, 61.88) * mm});
            skLineSegment(sketch, "E356", {"start": v(-1593.23, 61.88) * mm, "end": v(-1580.72, 65.68) * mm});
            skLineSegment(sketch, "E357", {"start": v(-1580.72, 65.68) * mm, "end": v(-1567.6, 66.98) * mm});
            skLineSegment(sketch, "E358", {"start": v(-862.12, -177.7) * mm, "end": v(-836.55, -177.7) * mm});
            skLineSegment(sketch, "E359", {"start": v(-836.55, -177.7) * mm, "end": v(-856.78, -234.4) * mm});
            skLineSegment(sketch, "E360", {"start": v(-856.78, -234.4) * mm, "end": v(-883.64, -234.4) * mm});
            skLineSegment(sketch, "E361", {"start": v(-883.64, -234.4) * mm, "end": v(-862.12, -177.7) * mm});
            skLineSegment(sketch, "E362", {"start": v(-668.37, -177.7) * mm, "end": v(-690.2, -177.7) * mm});
            skLineSegment(sketch, "E363", {"start": v(-690.2, -177.7) * mm, "end": v(-707.23, -234.4) * mm});
            skLineSegment(sketch, "E364", {"start": v(-707.23, -234.4) * mm, "end": v(-667.32, -206.58) * mm});
            skLineSegment(sketch, "E365", {"start": v(-667.32, -206.58) * mm, "end": v(-668.37, -177.7) * mm});
            skSolve(sketch);
        }
        {
            var Q0;
            Q0=makeQuery(id+"F0.imprint","IMPRINT",FACE,{"disambiguationData":[TD([[makeQuery(id+"F0.imprint","IMPRINT",EDGE,{"derivedFrom":sQuery(id+"F0.wireOp",EDGE,"E0")}),1.0]])]});
            var Q1;
            Q1=makeQuery(id+"F0.imprint","IMPRINT",FACE,{"disambiguationData":[TD([[makeQuery(id+"F0.imprint","IMPRINT",EDGE,{"derivedFrom":sQuery(id+"F0.wireOp",EDGE,"E309")}),1.0]])]});
            var Q2;
            Q2=makeQuery(id+"F0.imprint","IMPRINT",FACE,{"disambiguationData":[TD([[makeQuery(id+"F0.imprint","IMPRINT",EDGE,{"derivedFrom":sQuery(id+"F0.wireOp",EDGE,"E358")}),-1.0]])]});
            var Q3;
            Q3=makeQuery(id+"F0.imprint","IMPRINT",FACE,{"disambiguationData":[TD([[makeQuery(id+"F0.imprint","IMPRINT",EDGE,{"derivedFrom":sQuery(id+"F0.wireOp",EDGE,"E362")}),1.0]])]});
            extrude(context, id + "F1", {"entities" : qUnion([Q0, Q1, Q2, Q3]), "depth" : 1.5 * mm});
        }
    });
